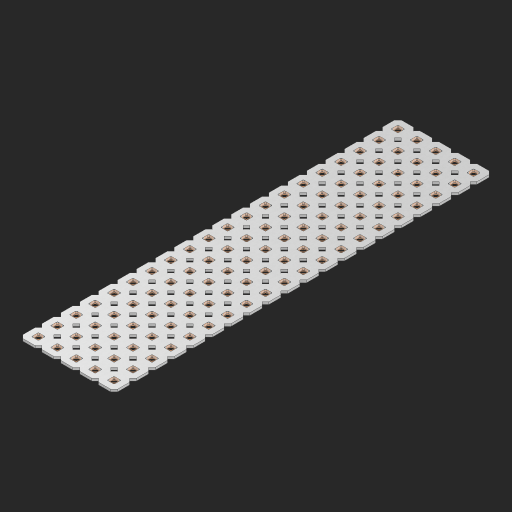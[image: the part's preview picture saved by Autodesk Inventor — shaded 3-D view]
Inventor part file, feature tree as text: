
AUTODESK INVENTOR PART (.ipt)
format: ipt  version: 2023 (Build 270158000, 158)  size: 1,433,600 bytes
history: native  units: in
note: dims shown in document units (in); Inventor stores cm internally (conversion verified against a paired STEP export)
features: other x101, extrude x99, sketch x2, pattern_linear x1
ambient origin geometry x8: Origin, YZ Plane, XZ Plane, XY Plane, X Axis, Y Axis, Z Axis, Center Point
bodies: Solid1 (feature_tree), Body (feature_tree)
feature tree (203):
  pattern_linear  "Rectangular Pattern1"  Spacing1=0.09in  [1 undecoded]
  sketch  "Sketch1"  dims[d1=0.5in]
  sketch  "Sketch2"  dims[d2=0.182in d3=0.09in d4=0.09in d5=0.09in d6=0.09in d7=0.09in d8=0.09in d9=0.09in d10=0.09in d11=0.02in d13=0.0in d14=0.172in d15=0.0625in d16=0.0in d19=0.5in d22=0.5in]
  other  "Srf1"
  other  "Srf126"
  other  "Srf127"
  other  "Srf128"
  other  "Srf129"
  other  "Srf130"
  other  "Srf131"
  other  "Srf250"
  other  "Srf251"
  other  "Srf252"
  other  "Srf253"
  other  "Srf254"
  other  "Srf255"
  other  "Srf256"
  other  "Srf257"
  other  "Srf258"
  other  "Srf259"
  other  "Srf260"
  other  "Srf261"
  other  "Srf262"
  other  "Srf268"
  other  "Srf269"
  other  "Srf270"
  other  "Srf271"
  other  "Srf272"
  other  "Srf273"
  other  "Srf274"
  other  "Srf275"
  other  "Srf276"
  other  "Srf277"
  other  "Srf278"
  other  "Srf279"
  other  "Srf280"
  other  "Srf281"
  other  "Srf282"
  other  "Srf283"
  other  "Srf284"
  other  "Srf285"
  other  "Srf286"
  other  "Srf287"
  other  "Srf293"
  other  "Srf294"
  other  "Srf295"
  other  "Srf296"
  other  "Srf297"
  other  "Srf298"
  other  "Srf299"
  other  "Srf300"
  other  "Srf301"
  other  "Srf302"
  other  "Srf303"
  other  "Srf304"
  other  "Srf305"
  other  "Srf306"
  other  "Srf307"
  other  "Srf308"
  other  "Srf309"
  other  "Srf310"
  other  "Srf311"
  other  "Srf312"
  other  "Srf318"
  other  "Srf319"
  other  "Srf320"
  other  "Srf321"
  other  "Srf322"
  other  "Srf323"
  other  "Srf324"
  other  "Srf325"
  other  "Srf326"
  other  "Srf327"
  other  "Srf328"
  other  "Srf329"
  other  "Srf330"
  other  "Srf331"
  other  "Srf332"
  other  "Srf333"
  other  "Srf334"
  other  "Srf335"
  other  "Srf336"
  other  "Srf337"
  other  "Srf343"
  other  "Srf344"
  other  "Srf345"
  other  "Srf346"
  other  "Srf347"
  other  "Srf348"
  other  "Srf349"
  other  "Srf350"
  other  "Srf351"
  other  "Srf352"
  other  "Srf353"
  other  "Srf354"
  other  "Srf355"
  other  "Srf356"
  other  "Srf357"
  other  "Srf358"
  other  "Srf359"
  other  "Srf360"
  other  "Srf361"
  other  "Srf362"
  other  "Circle"
  extrude  "ExtrusionSrf126"  Depth=0.09in
  extrude  "ExtrusionSrf127"  Depth=0.09in
  extrude  "ExtrusionSrf128"  Depth=0.09in
  extrude  "ExtrusionSrf129"  Depth=0.09in
  extrude  "ExtrusionSrf130"  Depth=0.09in
  extrude  "ExtrusionSrf131"  Depth=0.09in
  extrude  "ExtrusionSrf250"  Depth=0.09in
  extrude  "ExtrusionSrf251"  Depth=0.02in
  extrude  "ExtrusionSrf252"  TaperAngle=0.0deg  [1 undecoded]
  extrude  "ExtrusionSrf253"  Depth=0.5in
  extrude  "ExtrusionSrf254"  Depth=0.0625in TaperAngle=0.0deg
  extrude  "ExtrusionSrf255"  Depth=0.5in
  extrude  "ExtrusionSrf256"  Depth=0.5in
  extrude  "ExtrusionSrf257"  [1 undecoded]
  extrude  "ExtrusionSrf258"  [1 undecoded]
  extrude  "ExtrusionSrf259"  [1 undecoded]
  extrude  "ExtrusionSrf260"  [1 undecoded]
  extrude  "ExtrusionSrf261"  [1 undecoded]
  extrude  "ExtrusionSrf262"  [1 undecoded]
  extrude  "ExtrusionSrf268"  [1 undecoded]
  extrude  "ExtrusionSrf269"  [1 undecoded]
  extrude  "ExtrusionSrf270"  [1 undecoded]
  extrude  "ExtrusionSrf271"  [1 undecoded]
  extrude  "ExtrusionSrf272"  [1 undecoded]
  extrude  "ExtrusionSrf273"  [1 undecoded]
  extrude  "ExtrusionSrf274"  [1 undecoded]
  extrude  "ExtrusionSrf275"  [1 undecoded]
  extrude  "ExtrusionSrf276"  [1 undecoded]
  extrude  "ExtrusionSrf277"  [1 undecoded]
  extrude  "ExtrusionSrf278"  [1 undecoded]
  extrude  "ExtrusionSrf279"  [1 undecoded]
  extrude  "ExtrusionSrf280"  [1 undecoded]
  extrude  "ExtrusionSrf281"  [1 undecoded]
  extrude  "ExtrusionSrf282"  [1 undecoded]
  extrude  "ExtrusionSrf283"  [1 undecoded]
  extrude  "ExtrusionSrf284"  [1 undecoded]
  extrude  "ExtrusionSrf285"  [1 undecoded]
  extrude  "ExtrusionSrf286"  [1 undecoded]
  extrude  "ExtrusionSrf287"  [1 undecoded]
  extrude  "ExtrusionSrf293"  [1 undecoded]
  extrude  "ExtrusionSrf294"  [1 undecoded]
  extrude  "ExtrusionSrf295"  [1 undecoded]
  extrude  "ExtrusionSrf296"  [1 undecoded]
  extrude  "ExtrusionSrf297"  [1 undecoded]
  extrude  "ExtrusionSrf298"  [1 undecoded]
  extrude  "ExtrusionSrf299"  [1 undecoded]
  extrude  "ExtrusionSrf300"  [1 undecoded]
  extrude  "ExtrusionSrf301"  [1 undecoded]
  extrude  "ExtrusionSrf302"  [1 undecoded]
  extrude  "ExtrusionSrf303"  [1 undecoded]
  extrude  "ExtrusionSrf304"  [1 undecoded]
  extrude  "ExtrusionSrf305"  [1 undecoded]
  extrude  "ExtrusionSrf306"  [1 undecoded]
  extrude  "ExtrusionSrf307"  [1 undecoded]
  extrude  "ExtrusionSrf308"  [1 undecoded]
  extrude  "ExtrusionSrf309"  [1 undecoded]
  extrude  "ExtrusionSrf310"  [1 undecoded]
  extrude  "ExtrusionSrf311"  [1 undecoded]
  extrude  "ExtrusionSrf312"  [1 undecoded]
  extrude  "ExtrusionSrf318"  [1 undecoded]
  extrude  "ExtrusionSrf319"  [1 undecoded]
  extrude  "ExtrusionSrf320"  [1 undecoded]
  extrude  "ExtrusionSrf321"  [1 undecoded]
  extrude  "ExtrusionSrf322"  [1 undecoded]
  extrude  "ExtrusionSrf323"  [1 undecoded]
  extrude  "ExtrusionSrf324"  [1 undecoded]
  extrude  "ExtrusionSrf325"  [1 undecoded]
  extrude  "ExtrusionSrf326"  [1 undecoded]
  extrude  "ExtrusionSrf327"  [1 undecoded]
  extrude  "ExtrusionSrf328"  [1 undecoded]
  extrude  "ExtrusionSrf329"  [1 undecoded]
  extrude  "ExtrusionSrf330"  [1 undecoded]
  extrude  "ExtrusionSrf331"  [1 undecoded]
  extrude  "ExtrusionSrf332"  [1 undecoded]
  extrude  "ExtrusionSrf333"  [1 undecoded]
  extrude  "ExtrusionSrf334"  [1 undecoded]
  extrude  "ExtrusionSrf335"  [1 undecoded]
  extrude  "ExtrusionSrf336"  [1 undecoded]
  extrude  "ExtrusionSrf337"  [1 undecoded]
  extrude  "ExtrusionSrf343"  [1 undecoded]
  extrude  "ExtrusionSrf344"  [1 undecoded]
  extrude  "ExtrusionSrf345"  [1 undecoded]
  extrude  "ExtrusionSrf346"  [1 undecoded]
  extrude  "ExtrusionSrf347"  [1 undecoded]
  extrude  "ExtrusionSrf348"  [1 undecoded]
  extrude  "ExtrusionSrf349"  [1 undecoded]
  extrude  "ExtrusionSrf350"  [1 undecoded]
  extrude  "ExtrusionSrf351"  [1 undecoded]
  extrude  "ExtrusionSrf352"  [1 undecoded]
  extrude  "ExtrusionSrf353"  [1 undecoded]
  extrude  "ExtrusionSrf354"  [1 undecoded]
  extrude  "ExtrusionSrf355"  [1 undecoded]
  extrude  "ExtrusionSrf356"  [1 undecoded]
  extrude  "ExtrusionSrf357"  [1 undecoded]
  extrude  "ExtrusionSrf358"  [1 undecoded]
  extrude  "ExtrusionSrf359"  [1 undecoded]
  extrude  "ExtrusionSrf360"  [1 undecoded]
  extrude  "ExtrusionSrf361"  [1 undecoded]
  extrude  "ExtrusionSrf362"  [1 undecoded]
note: 88 required parameter values undecoded (feature->parameter linkage not recoverable at this tier; creation-order binding heuristic only, values carry confidence <= 0.55)
